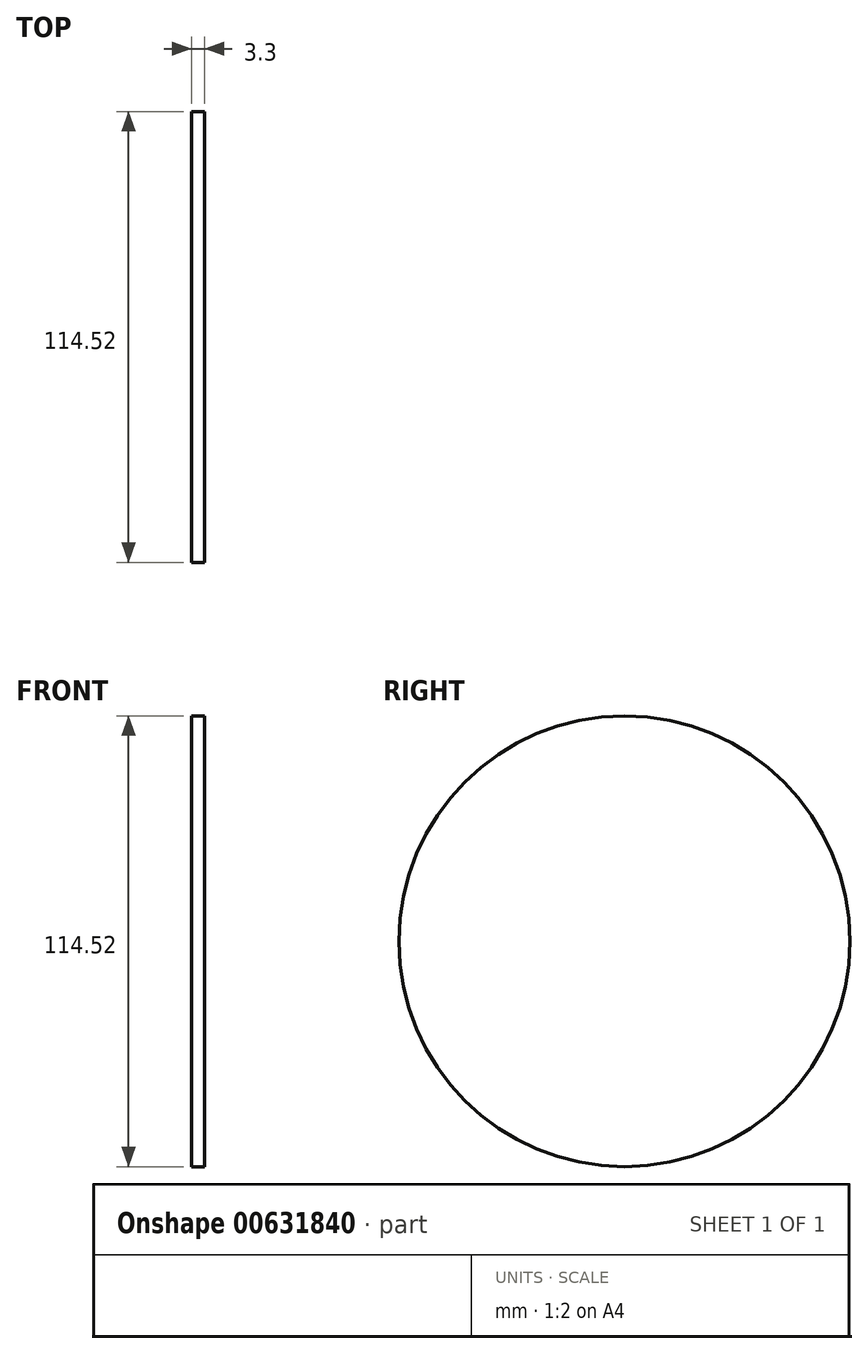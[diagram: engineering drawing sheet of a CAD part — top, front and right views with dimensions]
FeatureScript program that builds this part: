
annotation { "Feature Type Name" : "Feature", "Feature Type Description" : "" }
export const myFeature = defineFeature(function(context is Context, id is Id, definition is map)
    precondition{}
    {
        {
            var Q0;
            Q0=qCreatedBy(makeId("Right.planeOp"),FACE);
            var sketch = newSketch(context, id + "F0", { "sketchPlane" : qUnion([Q0])});
            skCircle(sketch, "E0", {"center": v(0, 0) * mm, "radius": 57.26 * mm});
            skCircle(sketch, "E1", {"center": v(0, 0) * mm, "radius": 24.14 * mm});
            skSolve(sketch);
        }
        {
            var Q0;
            Q0=sQuery(id+"F0.wireOp",EDGE,"E0");
            extrude(context, id + "F1", {"bodyType" : ToolBodyType.SURFACE, "surfaceEntities" : qUnion([Q0]), "depth" : 3.3 * mm, "offsetDistance" : 25.4 * mm});
        }
    });
